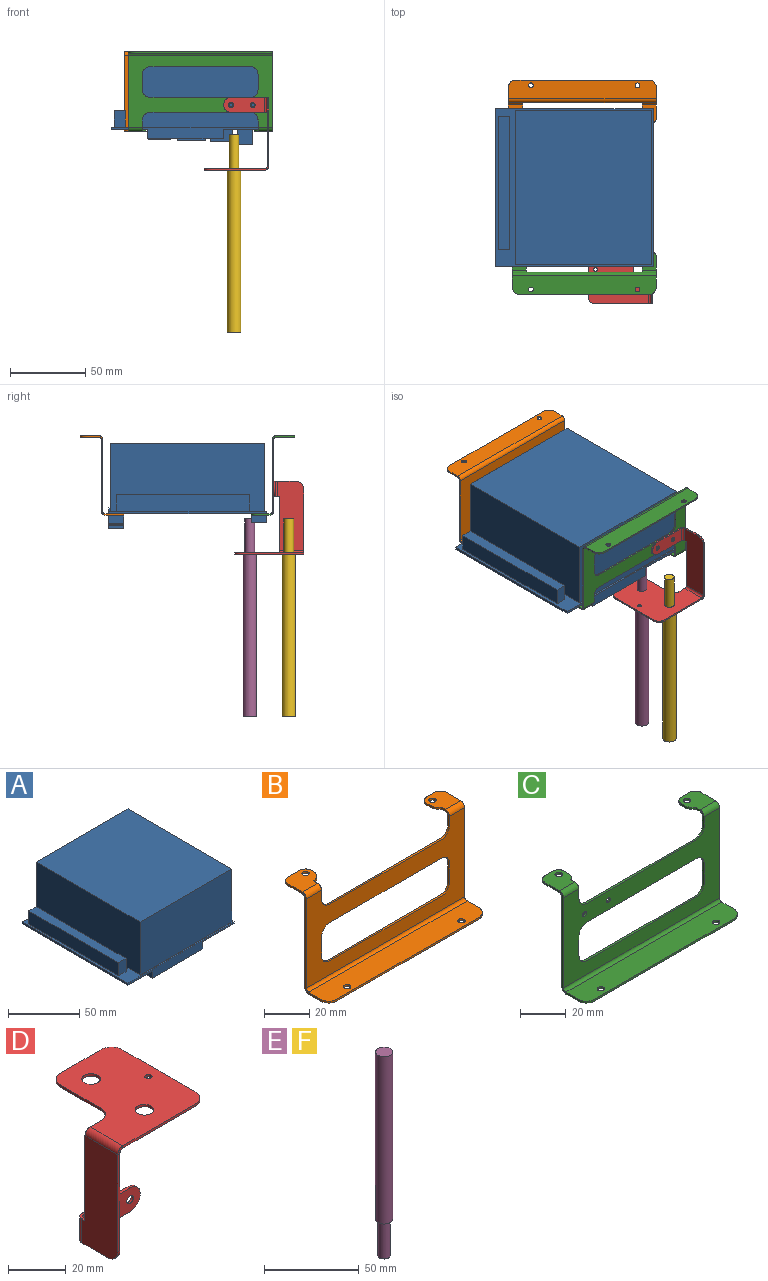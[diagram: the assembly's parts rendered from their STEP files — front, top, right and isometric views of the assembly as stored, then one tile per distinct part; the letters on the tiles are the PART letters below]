
ASSEMBLY  parts=6 mates=5
PART A: 47 faces, bbox 105x105x57 mm
  f0: plane 105x105mm, normal (0,0,1), area 979.1mm2, adj f2,f3,f4,f5,f6,f7,f8,f9
  f1: plane 105x105mm, normal (0,0,-1), area 9924.6mm2, adj f3,f4,f5,f6,f16,f18,f20,f22
  f2: plane 91x45.46mm, normal (0,1,0), area 4103.2mm2, adj f0,f8,f9,f10,f32,f33,f34
  f3: plane 105x7.75mm, normal (0,-1,0), area 474.1mm2, adj f0,f1,f4,f6,f24,f26,f27
  f4: plane 105x1.57mm, normal (1,0,0), area 164.8mm2, adj f0,f1,f3,f5
  f5: plane 105x13.92mm, normal (0,1,0), area 637.9mm2, adj f0,f1,f4,f6,f28,f29,f31,f32
  f6: plane 105x1.57mm, normal (-1,0,0), area 164.8mm2, adj f0,f1,f3,f5
  f7: plane 91x45.46mm, normal (0,-1,0), area 4136.9mm2, adj f0,f8,f9,f10
  f8: plane 103x45.46mm, normal (1,0,0), area 4682.4mm2, adj f0,f2,f7,f10
  f9: plane 103x45.46mm, normal (-1,0,0), area 4682.4mm2, adj f0,f2,f7,f10
  f10: plane 103x91mm, normal (0,0,1), area 9373mm2, adj f2,f7,f8,f9
  f11: plane 11.16x7.4mm, normal (0,1,0), area 82.6mm2, adj f0,f12,f14,f15
  f12: plane 89x11.16mm, normal (-1,0,0), area 992.9mm2, adj f0,f11,f13,f15
  f13: plane 11.16x7.4mm, normal (0,-1,0), area 82.6mm2, adj f0,f12,f14,f15
  f14: plane 89x11.16mm, normal (1,0,0), area 992.9mm2, adj f0,f11,f13,f15
  f15: plane 89x7.4mm, normal (0,0,1), area 658.6mm2, adj f11,f12,f13,f14
  f16: cylinder r=1.25mm len=2.5mm, axis (0,0,1), area 12.3mm2, adj f1,f17
  f17: plane 2.5x2.5mm, normal (0,0,-1), area 4.9mm2, adj f16
  f18: cylinder r=1.25mm len=2.5mm, axis (0,0,1), area 12.3mm2, adj f1,f19
  f19: plane 2.5x2.5mm, normal (0,0,-1), area 4.9mm2, adj f18
  f20: cylinder r=1.25mm len=2.5mm, axis (0,0,1), area 12.3mm2, adj f1,f21
  f21: plane 2.5x2.5mm, normal (0,0,-1), area 4.9mm2, adj f20
  f22: cylinder r=1.25mm len=2.5mm, axis (0,0,1), area 12.3mm2, adj f1,f23
  f23: plane 2.5x2.5mm, normal (0,0,-1), area 4.9mm2, adj f22
  f24: plane 10x6.18mm, normal (-1,0,0), area 61.8mm2, adj f1,f3,f25,f27
  f25: plane 50.08x6.18mm, normal (0,1,0), area 309.3mm2, adj f1,f24,f26,f27
  f26: plane 10x6.18mm, normal (1,0,0), area 61.8mm2, adj f1,f3,f25,f27
  f27: plane 50.08x10mm, normal (0,0,-1), area 500.8mm2, adj f3,f24,f25,f26
  f28: plane 10x10mm, normal (-1,0,0), area 100mm2, adj f1,f5,f30,f31
  f29: plane 10x10mm, normal (1,0,0), area 100mm2, adj f1,f5,f30,f31
  f30: plane 10x10mm, normal (0,-1,0), area 100mm2, adj f1,f28,f29,f31
  f31: plane 10x10mm, normal (0,0,-1), area 100mm2, adj f5,f28,f29,f30
  f32: plane 14.3x1mm, normal (0,0,1), area 14.3mm2, adj f2,f5,f33,f34
  f33: plane 2.35x1mm, normal (-1,0,0), area 2.4mm2, adj f0,f2,f5,f32
  f34: plane 2.35x1mm, normal (1,0,0), area 2.4mm2, adj f0,f2,f5,f32
  f35: plane 14.3x7.76mm, normal (0,-1,0), area 111mm2, adj f1,f36,f37,f38
  f36: plane 10x7.76mm, normal (1,0,0), area 77.6mm2, adj f1,f5,f35,f38
  f37: plane 10x7.76mm, normal (-1,0,0), area 77.6mm2, adj f1,f5,f35,f38
  f38: plane 14.3x10mm, normal (0,0,-1), area 143mm2, adj f5,f35,f36,f37
  f39: plane 10x6.96mm, normal (1,0,0), area 69.6mm2, adj f1,f5,f40,f42
  f40: plane 18.7x6.96mm, normal (0,-1,0), area 130.1mm2, adj f1,f39,f41,f42
  f41: plane 10x6.96mm, normal (-1,0,0), area 69.6mm2, adj f1,f5,f40,f42
  f42: plane 18.7x10mm, normal (0,0,-1), area 187mm2, adj f5,f39,f40,f41
  f43: plane 10x6.56mm, normal (1,0,0), area 65.6mm2, adj f1,f5,f44,f46
  f44: plane 15x6.56mm, normal (0,-1,0), area 98.3mm2, adj f1,f43,f45,f46
  f45: plane 10x6.56mm, normal (-1,0,0), area 65.6mm2, adj f1,f5,f44,f46
  f46: plane 15x10mm, normal (0,0,-1), area 150mm2, adj f5,f43,f44,f45
PART B: 58 faces, bbox 98.5x29x53 mm
  f0: plane 48x1mm, normal (1,0,0), area 48mm2, adj f9,f10,f28,f54
  f1: plane 48x1mm, normal (-1,0,0), area 48mm2, adj f9,f10,f41,f55
  f2: plane 5x1mm, normal (1,0,0), area 5mm2, adj f9,f10,f13,f42
  f3: plane 69.5x1mm, normal (0,0,1), area 69.5mm2, adj f9,f10,f13,f14
  f4: plane 5x1mm, normal (-1,0,0), area 5mm2, adj f9,f10,f14,f27
  f5: plane 69.5x1mm, normal (0,0,-1), area 69.5mm2, adj f9,f10,f15,f16
  f6: plane 10.5x1mm, normal (1,0,0), area 10.5mm2, adj f9,f10,f12,f15
  f7: plane 69.5x1mm, normal (0,0,1), area 69.5mm2, adj f9,f10,f11,f12
  f8: plane 10.5x1mm, normal (-1,0,0), area 10.5mm2, adj f9,f10,f11,f16
  f9: plane 98.5x48mm, normal (0,1,0), area 2335.4mm2, adj f0,f1,f2,f3,f4,f5,f6,f7
  f10: plane 98.5x48mm, normal (0,-1,0), area 2335.4mm2, adj f0,f1,f2,f3,f4,f5,f6,f7
  f11: cylinder r=5mm len=5mm, axis (0,-1,0), area 7.9mm2, adj f7,f8,f9,f10
  f12: cylinder r=5mm len=5mm, axis (0,-1,0), area 7.9mm2, adj f6,f7,f9,f10
  f13: cylinder r=5mm len=5mm, axis (0,-1,0), area 7.9mm2, adj f2,f3,f9,f10
  f14: cylinder r=5mm len=5mm, axis (0,-1,0), area 7.9mm2, adj f3,f4,f9,f10
  f15: cylinder r=5mm len=5mm, axis (0,-1,0), area 7.9mm2, adj f5,f6,f9,f10
  f16: cylinder r=5mm len=5mm, axis (0,-1,0), area 7.9mm2, adj f5,f8,f9,f10
  f17: plane 5x1mm, normal (0,1,0), area 5mm2, adj f22,f23,f25,f26
  f18: plane 9x1mm, normal (1,0,0), area 9mm2, adj f22,f23,f26,f28
  f19: plane 2.5x1mm, normal (-1,0,0), area 2.5mm2, adj f22,f23,f24,f27
  f20: cylinder r=1.6mm len=3.2mm, axis (0,0,-1), area 10.1mm2, adj f22,f23
  f21: plane 2.17x1mm, normal (-1,0,0), area 2.2mm2, adj f22,f23,f24,f25
  f22: plane 12.5x12mm, normal (0,0,-1), area 127.3mm2, adj f17,f18,f19,f20,f21,f24,f25,f26
  f23: plane 12.5x12mm, normal (0,0,1), area 127.3mm2, adj f17,f18,f19,f20,f21,f24,f25,f26
  f24: cylinder r=5mm len=4.33mm, axis (0,0,-1), area 5.2mm2, adj f19,f21,f22,f23
  f25: cylinder r=3.5mm len=3.5mm, axis (0,0,1), area 5.5mm2, adj f17,f21,f22,f23
  f26: cylinder r=3.5mm len=3.5mm, axis (0,0,1), area 5.5mm2, adj f17,f18,f22,f23
  f27: plane 2.5x2.5mm, normal (-1,0,0), area 3.1mm2, adj f4,f19,f29,f30
  f28: plane 2.5x2.5mm, normal (1,0,0), area 3.1mm2, adj f0,f18,f29,f30
  f29: cylinder r=2.5mm len=9.5mm, axis (-1,0,0), area 37.3mm2, adj f10,f23,f27,f28
  f30: cylinder r=1.5mm len=9.5mm, axis (-1,0,0), area 22.4mm2, adj f9,f22,f27,f28
  f31: plane 2.5x1mm, normal (1,0,0), area 2.5mm2, adj f36,f37,f39,f42
  f32: plane 9x1mm, normal (-1,0,0), area 9mm2, adj f36,f37,f40,f41
  f33: plane 7.5x1mm, normal (0,1,0), area 7.5mm2, adj f36,f37,f38,f40
  f34: cylinder r=1.6mm len=3.2mm, axis (0,0,-1), area 10.1mm2, adj f36,f37
  f35: plane 1.5x1mm, normal (1,0,0), area 1.5mm2, adj f36,f37,f38,f39
  f36: plane 14.5x12.5mm, normal (0,0,-1), area 150.1mm2, adj f31,f32,f33,f34,f35,f38,f39,f40
  f37: plane 14.5x12.5mm, normal (0,0,1), area 150.1mm2, adj f31,f32,f33,f34,f35,f38,f39,f40
  f38: cylinder r=3.5mm len=3.5mm, axis (0,0,1), area 5.5mm2, adj f33,f35,f36,f37
  f39: cylinder r=5mm len=5mm, axis (0,0,1), area 7.9mm2, adj f31,f35,f36,f37
  f40: cylinder r=3.5mm len=3.5mm, axis (0,0,1), area 5.5mm2, adj f32,f33,f36,f37
  f41: plane 2.5x2.5mm, normal (-1,0,0), area 3.1mm2, adj f1,f32,f43,f44
  f42: plane 2.5x2.5mm, normal (1,0,0), area 3.1mm2, adj f2,f31,f43,f44
  f43: cylinder r=2.5mm len=9.5mm, axis (-1,0,0), area 37.3mm2, adj f10,f37,f41,f42
  f44: cylinder r=1.5mm len=9.5mm, axis (-1,0,0), area 22.4mm2, adj f9,f36,f41,f42
  f45: plane 88.5x1mm, normal (0,-1,0), area 88.5mm2, adj f50,f51,f52,f53
  f46: plane 7.5x1mm, normal (-1,0,0), area 7.5mm2, adj f50,f51,f52,f55
  f47: cylinder r=1.6mm len=3.2mm, axis (0,0,-1), area 10.1mm2, adj f50,f51
  f48: cylinder r=1.6mm len=3.2mm, axis (0,0,-1), area 10.1mm2, adj f50,f51
  f49: plane 7.5x1mm, normal (1,0,0), area 7.5mm2, adj f50,f51,f53,f54
  f50: plane 98.5x12.5mm, normal (0,0,-1), area 1204.4mm2, adj f45,f46,f47,f48,f49,f52,f53,f56
  f51: plane 98.5x12.5mm, normal (0,0,1), area 1204.4mm2, adj f45,f46,f47,f48,f49,f52,f53,f57
  f52: cylinder r=5mm len=5mm, axis (0,0,1), area 7.9mm2, adj f45,f46,f50,f51
  f53: cylinder r=5mm len=5mm, axis (0,0,1), area 7.9mm2, adj f45,f49,f50,f51
  f54: plane 2.5x2.5mm, normal (1,0,0), area 3.1mm2, adj f0,f49,f56,f57
  f55: plane 2.5x2.5mm, normal (-1,0,0), area 3.1mm2, adj f1,f46,f56,f57
  f56: cylinder r=2.5mm len=98.5mm, axis (1,0,0), area 386.8mm2, adj f9,f50,f54,f55
  f57: cylinder r=1.5mm len=98.5mm, axis (1,0,0), area 232.1mm2, adj f10,f51,f54,f55
PART C: 60 faces, bbox 96x29x53 mm
  f0: plane 48x1mm, normal (1,0,0), area 48mm2, adj f11,f12,f30,f56
  f1: plane 48x1mm, normal (-1,0,0), area 48mm2, adj f11,f12,f43,f57
  f2: plane 5x1mm, normal (1,0,0), area 5mm2, adj f11,f12,f14,f44
  f3: plane 67x1mm, normal (0,0,1), area 67mm2, adj f11,f12,f13,f14
  f4: plane 5x1mm, normal (-1,0,0), area 5mm2, adj f11,f12,f13,f29
  f5: plane 67x1mm, normal (0,0,-1), area 67mm2, adj f11,f12,f16,f18
  f6: plane 10.5x1mm, normal (1,0,0), area 10.5mm2, adj f11,f12,f15,f16
  f7: plane 67x1mm, normal (0,0,1), area 67mm2, adj f11,f12,f15,f17
  f8: cylinder r=1.25mm len=2.5mm, axis (0,-1,0), area 7.9mm2, adj f11,f12
  f9: cylinder r=1.25mm len=2.5mm, axis (0,-1,0), area 7.9mm2, adj f11,f12
  f10: plane 10.5x1mm, normal (-1,0,0), area 10.5mm2, adj f11,f12,f17,f18
  f11: plane 96x48mm, normal (0,1,0), area 2281.9mm2, adj f0,f1,f2,f3,f4,f5,f6,f7
  f12: plane 96x48mm, normal (0,-1,0), area 2281.9mm2, adj f0,f1,f2,f3,f4,f5,f6,f7
  f13: cylinder r=5mm len=5mm, axis (0,-1,0), area 7.9mm2, adj f3,f4,f11,f12
  f14: cylinder r=5mm len=5mm, axis (0,-1,0), area 7.9mm2, adj f2,f3,f11,f12
  f15: cylinder r=5mm len=5mm, axis (0,-1,0), area 7.9mm2, adj f6,f7,f11,f12
  f16: cylinder r=5mm len=5mm, axis (0,-1,0), area 7.9mm2, adj f5,f6,f11,f12
  f17: cylinder r=5mm len=5mm, axis (0,-1,0), area 7.9mm2, adj f7,f10,f11,f12
  f18: cylinder r=5mm len=5mm, axis (0,-1,0), area 7.9mm2, adj f5,f10,f11,f12
  f19: plane 5x1mm, normal (0,1,0), area 5mm2, adj f24,f25,f27,f28
  f20: plane 9x1mm, normal (1,0,0), area 9mm2, adj f24,f25,f28,f30
  f21: plane 2.5x1mm, normal (-1,0,0), area 2.5mm2, adj f24,f25,f26,f29
  f22: cylinder r=1.6mm len=3.2mm, axis (0,0,-1), area 10.1mm2, adj f24,f25
  f23: plane 2.17x1mm, normal (-1,0,0), area 2.2mm2, adj f24,f25,f26,f27
  f24: plane 12.5x12mm, normal (0,0,-1), area 127.3mm2, adj f19,f20,f21,f22,f23,f26,f27,f28
  f25: plane 12.5x12mm, normal (0,0,1), area 127.3mm2, adj f19,f20,f21,f22,f23,f26,f27,f28
  f26: cylinder r=5mm len=4.33mm, axis (0,0,-1), area 5.2mm2, adj f21,f23,f24,f25
  f27: cylinder r=3.5mm len=3.5mm, axis (0,0,1), area 5.5mm2, adj f19,f23,f24,f25
  f28: cylinder r=3.5mm len=3.5mm, axis (0,0,1), area 5.5mm2, adj f19,f20,f24,f25
  f29: plane 2.5x2.5mm, normal (-1,0,0), area 3.1mm2, adj f4,f21,f31,f32
  f30: plane 2.5x2.5mm, normal (1,0,0), area 3.1mm2, adj f0,f20,f31,f32
  f31: cylinder r=2.5mm len=9.5mm, axis (-1,0,0), area 37.3mm2, adj f12,f25,f29,f30
  f32: cylinder r=1.5mm len=9.5mm, axis (-1,0,0), area 22.4mm2, adj f11,f24,f29,f30
  f33: plane 2.5x1mm, normal (1,0,0), area 2.5mm2, adj f38,f39,f40,f44
  f34: plane 9x1mm, normal (-1,0,0), area 9mm2, adj f38,f39,f42,f43
  f35: plane 5x1mm, normal (0,1,0), area 5mm2, adj f38,f39,f41,f42
  f36: cylinder r=1.6mm len=3.2mm, axis (0,0,-1), area 10.1mm2, adj f38,f39
  f37: plane 2.17x1mm, normal (1,0,0), area 2.2mm2, adj f38,f39,f40,f41
  f38: plane 12.5x12mm, normal (0,0,-1), area 127.3mm2, adj f33,f34,f35,f36,f37,f40,f41,f42
  f39: plane 12.5x12mm, normal (0,0,1), area 127.3mm2, adj f33,f34,f35,f36,f37,f40,f41,f42
  f40: cylinder r=5mm len=4.33mm, axis (0,0,-1), area 5.2mm2, adj f33,f37,f38,f39
  f41: cylinder r=3.5mm len=3.5mm, axis (0,0,1), area 5.5mm2, adj f35,f37,f38,f39
  f42: cylinder r=3.5mm len=3.5mm, axis (0,0,1), area 5.5mm2, adj f34,f35,f38,f39
  f43: plane 2.5x2.5mm, normal (-1,0,0), area 3.1mm2, adj f1,f34,f45,f46
  f44: plane 2.5x2.5mm, normal (1,0,0), area 3.1mm2, adj f2,f33,f45,f46
  f45: cylinder r=2.5mm len=9.5mm, axis (-1,0,0), area 37.3mm2, adj f12,f39,f43,f44
  f46: cylinder r=1.5mm len=9.5mm, axis (-1,0,0), area 22.4mm2, adj f11,f38,f43,f44
  f47: plane 86x1mm, normal (0,-1,0), area 86mm2, adj f52,f53,f54,f55
  f48: plane 7.5x1mm, normal (-1,0,0), area 7.5mm2, adj f52,f53,f55,f57
  f49: cylinder r=1.6mm len=3.2mm, axis (0,0,-1), area 10.1mm2, adj f52,f53
  f50: cylinder r=1.6mm len=3.2mm, axis (0,0,-1), area 10.1mm2, adj f52,f53
  f51: plane 7.5x1mm, normal (1,0,0), area 7.5mm2, adj f52,f53,f54,f56
  f52: plane 96x12.5mm, normal (0,0,-1), area 1173.2mm2, adj f47,f48,f49,f50,f51,f54,f55,f58
  f53: plane 96x12.5mm, normal (0,0,1), area 1173.2mm2, adj f47,f48,f49,f50,f51,f54,f55,f59
  f54: cylinder r=5mm len=5mm, axis (0,0,1), area 7.9mm2, adj f47,f51,f52,f53
  f55: cylinder r=5mm len=5mm, axis (0,0,1), area 7.9mm2, adj f47,f48,f52,f53
  f56: plane 2.5x2.5mm, normal (1,0,0), area 3.1mm2, adj f0,f51,f58,f59
  f57: plane 2.5x2.5mm, normal (-1,0,0), area 3.1mm2, adj f1,f48,f58,f59
  f58: cylinder r=2.5mm len=96mm, axis (1,0,0), area 377mm2, adj f11,f52,f56,f57
  f59: cylinder r=1.5mm len=96mm, axis (1,0,0), area 226.2mm2, adj f12,f53,f56,f57
PART D: 36 faces, bbox 43x46x48.5 mm
  f0: plane 22.5x1mm, normal (0,0,-1), area 22.5mm2, adj f4,f5,f6,f32
  f1: plane 22.5x1mm, normal (0,0,1), area 22.5mm2, adj f4,f5,f6,f33
  f2: cylinder r=1.6mm len=3.2mm, axis (0,-1,0), area 10.1mm2, adj f4,f5
  f3: cylinder r=1.6mm len=3.2mm, axis (0,-1,0), area 10.1mm2, adj f4,f5
  f4: plane 27.5x10mm, normal (0,1,0), area 248.2mm2, adj f0,f1,f2,f3,f6,f34
  f5: plane 27.5x10mm, normal (0,-1,0), area 248.2mm2, adj f0,f1,f2,f3,f6,f35
  f6: cylinder r=5mm len=10mm, axis (0,-1,0), area 15.7mm2, adj f0,f1,f4,f5
  f7: plane 41x1mm, normal (0,-1,0), area 41mm2, adj f11,f12,f13,f28
  f8: plane 36x1mm, normal (0,1,0), area 36mm2, adj f9,f11,f12,f29
  f9: plane 1.5x1mm, normal (0,0,1), area 1.5mm2, adj f8,f11,f12,f33
  f10: plane 12.5x1mm, normal (0,0,-1), area 12.5mm2, adj f11,f12,f13,f32
  f11: plane 46x17.5mm, normal (-1,0,0), area 745.6mm2, adj f7,f8,f9,f10,f13,f30,f34
  f12: plane 46x17.5mm, normal (1,0,0), area 745.6mm2, adj f7,f8,f9,f10,f13,f31,f35
  f13: cylinder r=5mm len=5mm, axis (-1,0,0), area 7.9mm2, adj f7,f10,f11,f12
  f14: plane 35.5x1mm, normal (0,-1,0), area 35.5mm2, adj f22,f23,f25,f28
  f15: plane 36x1mm, normal (1,0,0), area 36mm2, adj f22,f23,f25,f27
  f16: plane 20x1mm, normal (0,1,0), area 20mm2, adj f22,f23,f26,f27
  f17: plane 20x1mm, normal (-1,0,0), area 20mm2, adj f22,f23,f24,f26
  f18: cylinder r=1.25mm len=2.5mm, axis (0,0,1), area 7.9mm2, adj f22,f23
  f19: cylinder r=3.2mm len=6.4mm, axis (0,0,1), area 20.1mm2, adj f22,f23
  f20: cylinder r=3.2mm len=6.4mm, axis (0,0,1), area 20.1mm2, adj f22,f23
  f21: plane 5.5x1mm, normal (0,1,0), area 5.5mm2, adj f22,f23,f24,f29
  f22: plane 46x40.5mm, normal (0,0,1), area 1468mm2, adj f14,f15,f16,f17,f18,f19,f20,f21
  f23: plane 46x40.5mm, normal (0,0,-1), area 1468mm2, adj f14,f15,f16,f17,f18,f19,f20,f21
  f24: cylinder r=5mm len=5mm, axis (0,0,-1), area 7.9mm2, adj f17,f21,f22,f23
  f25: cylinder r=5mm len=5mm, axis (0,0,-1), area 7.9mm2, adj f14,f15,f22,f23
  f26: cylinder r=5mm len=5mm, axis (0,0,1), area 7.9mm2, adj f16,f17,f22,f23
  f27: cylinder r=5mm len=5mm, axis (0,0,1), area 7.9mm2, adj f15,f16,f22,f23
  f28: plane 2.5x2.5mm, normal (0,-1,0), area 3.1mm2, adj f7,f14,f30,f31
  f29: plane 2.5x2.5mm, normal (0,1,0), area 3.1mm2, adj f8,f21,f30,f31
  f30: cylinder r=2.5mm len=16mm, axis (0,-1,0), area 62.8mm2, adj f11,f22,f28,f29
  f31: cylinder r=1.5mm len=16mm, axis (0,-1,0), area 37.7mm2, adj f12,f23,f28,f29
  f32: plane 2.5x2.5mm, normal (0,0,-1), area 3.1mm2, adj f0,f10,f34,f35
  f33: plane 2.5x2.5mm, normal (0,0,1), area 3.1mm2, adj f1,f9,f34,f35
  f34: cylinder r=2.5mm len=10mm, axis (0,0,-1), area 39.3mm2, adj f4,f11,f32,f33
  f35: cylinder r=1.5mm len=10mm, axis (0,0,-1), area 23.6mm2, adj f5,f12,f32,f33
PART E: 5 faces, bbox 9x9x131.5 mm
  f0: cylinder r=3.2mm len=23.5mm, axis (0,0,1), area 472.5mm2, adj f2,f4
  f1: cylinder r=4.5mm len=108mm, axis (0,0,1), area 3053.6mm2, adj f2,f3
  f2: plane 9x9mm, normal (0,0,-1), area 31.4mm2, adj f0,f1
  f3: plane 9x9mm, normal (0,0,1), area 63.6mm2, adj f1
  f4: plane 6.4x6.4mm, normal (0,0,-1), area 32.2mm2, adj f0
PART F: same geometry as E
PLACE A at identity fixed
PLACE B rot(axis=(1,0,0),180deg) t=(6.5,56.5,50.43)mm
PLACE C rot(axis=(0,1,0),180deg) t=(6.5,-56.5,50.43)mm
PLACE D rot(axis=(0,1,0),180deg) t=(6.5,-56.5,50.43)mm
PLACE E rot(axis=(-1,0,0),180deg) t=(29,-41.5,-28.57)mm
PLACE F rot(axis=(-1,0,0),180deg) t=(29,-67.5,-28.57)mm
MATE fastened D.f3 <-> C.f9  axis (0,1,0) through (27,-57.5,14.93)mm
MATE fastened B.f20 <-> A.f22  axis (0,0,1) through (46,46,-1.57)mm
MATE fastened E.f1 <-> D.f19  axis (0,0,1) through (29,-41.5,-28.57)mm
MATE fastened C.f36 <-> A.f16  axis (0,0,1) through (46,-46,-1.57)mm
MATE fastened F.f1 <-> D.f20  axis (0,0,1) through (29,-67.5,-28.57)mm
